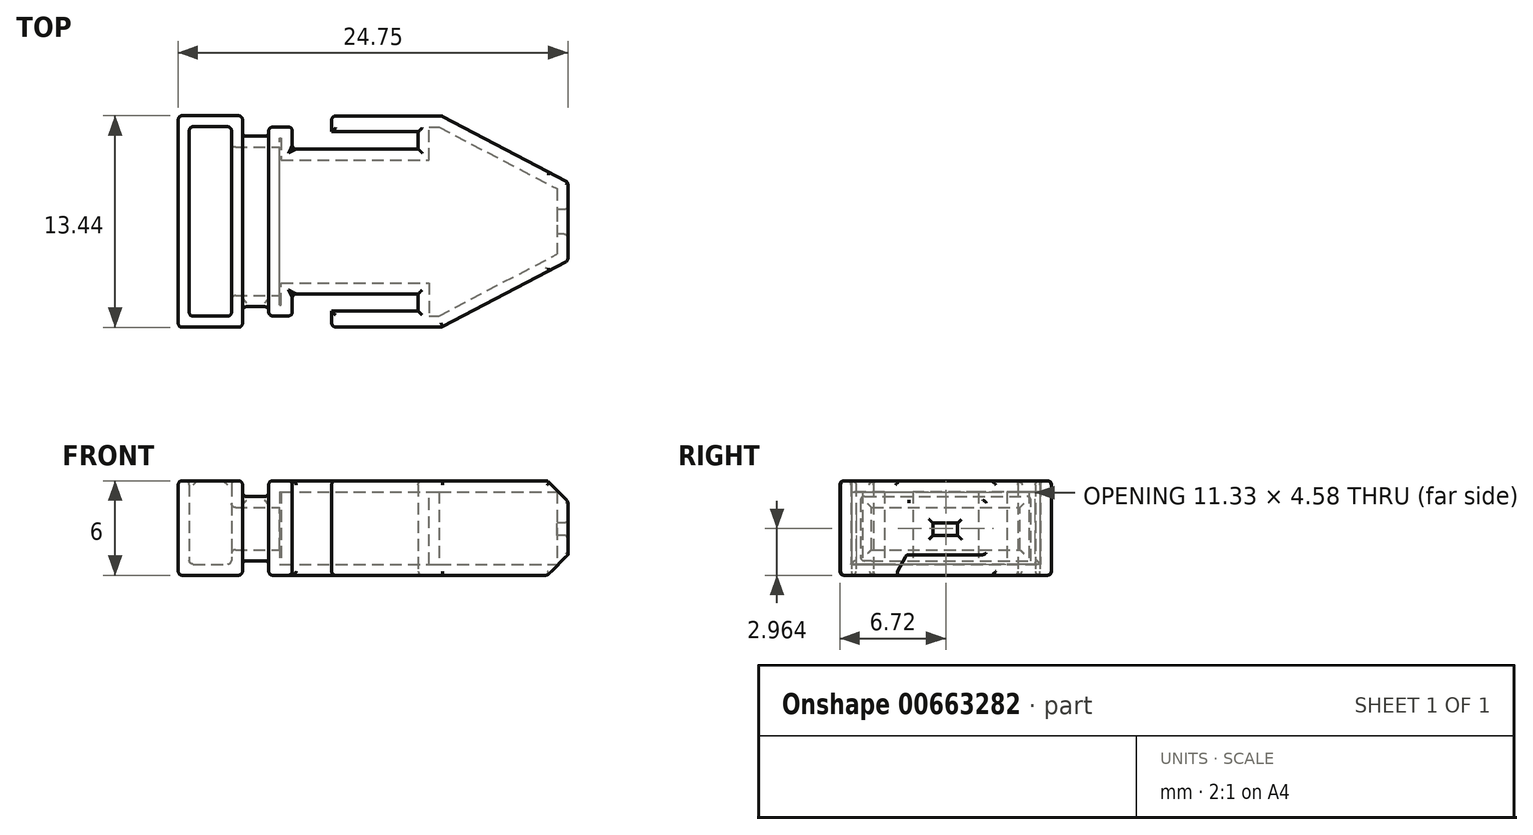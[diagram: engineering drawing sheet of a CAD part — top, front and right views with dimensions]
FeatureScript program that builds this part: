
annotation { "Feature Type Name" : "Feature", "Feature Type Description" : "" }
export const myFeature = defineFeature(function(context is Context, id is Id, definition is map)
    precondition{}
    {
        {
            var Q0;
            Q0=qCreatedBy(makeId("Top.planeOp"),FACE);
            var sketch = newSketch(context, id + "F0", { "sketchPlane" : qUnion([Q0])});
            skLineSegment(sketch, "E0", {"start": v(-19, 0) * mm, "end": v(-19, 6) * mm});
            skLineSegment(sketch, "E1", {"start": v(-19, 6) * mm, "end": v(-17.5, 6) * mm});
            skLineSegment(sketch, "E2", {"start": v(-17.5, 6) * mm, "end": v(-17.5, 4.6) * mm});
            skLineSegment(sketch, "E3", {"start": v(-17.5, 4.6) * mm, "end": v(-9.5, 4.6) * mm});
            skLineSegment(sketch, "E4", {"start": v(-9.5, 4.6) * mm, "end": v(-9.5, 5.7) * mm});
            skLineSegment(sketch, "E5", {"start": v(-9.5, 5.7) * mm, "end": v(-15, 5.7) * mm});
            skLineSegment(sketch, "E6", {"start": v(-15, 6.2) * mm, "end": v(-15, 5.7) * mm});
            skLineSegment(sketch, "E7", {"start": v(-15, 6.2) * mm, "end": v(-15, 6.2) * mm});
            skLineSegment(sketch, "E8", {"start": v(-15, 6.2) * mm, "end": v(-15, 6.7) * mm});
            skLineSegment(sketch, "E9", {"start": v(-15, 6.7) * mm, "end": v(-8, 6.7) * mm});
            skLineSegment(sketch, "E10", {"start": v(-8, 6.7) * mm, "end": v(0, 2.5) * mm});
            skLineSegment(sketch, "E11", {"start": v(0, 2.5) * mm, "end": v(0, 0) * mm});
            skLineSegment(sketch, "E12", {"start": v(0, 0) * mm, "end": v(-19, 0) * mm});
            skSolve(sketch);
        }
        {
            var Q0;
            Q0=makeQuery(id+"F0.imprint","IMPRINT",FACE,{"disambiguationData":[TD([[makeQuery(id+"F0.imprint","IMPRINT",EDGE,{"derivedFrom":sQuery(id+"F0.wireOp",EDGE,"E0")}),-1.0]])]});
            extrude(context, id + "F1", {"entities" : qUnion([Q0]), "depth" : 6 * mm, "offsetDistance" : 25 * mm});
        }
        {
            var Q0;
            Q0=makeQuery(id+"F1.opExtrude","SWEPT_FACE",FACE,{"disambiguationData":[OSD([sQuery(id+"F0.wireOp",EDGE,"E0")])]});
            var sketch = newSketch(context, id + "F2", { "sketchPlane" : qUnion([Q0])});
            skLineSegment(sketch, "E13.bottom", {"start": v(0, 0.92) * mm, "end": v(-5.41, 0.92) * mm});
            skLineSegment(sketch, "E13.top", {"start": v(0, 5) * mm, "end": v(-5.41, 5) * mm});
            skLineSegment(sketch, "E13.left", {"start": v(0, 0.92) * mm, "end": v(0, 5) * mm});
            skLineSegment(sketch, "E13.right", {"start": v(-5.41, 0.92) * mm, "end": v(-5.41, 5) * mm});
            skSolve(sketch);
        }
        {
            var Q0;
            Q0 = qSketchRegion(id + "F2", true);
            extrude(context, id + "F3", {"entities" : qUnion([Q0]), "operationType" : NewBodyOperationType.ADD, "depth" : 2 * mm, "offsetDistance" : 25 * mm});
        }
        {
            var Q0;
            Q0=qCreatedBy(makeId("Top.planeOp"),FACE);
            var sketch = newSketch(context, id + "F4", { "sketchPlane" : qUnion([Q0])});
            skLineSegment(sketch, "E14.bottom", {"start": v(-24.75, 6.72) * mm, "end": v(-20.67, 6.72) * mm});
            skLineSegment(sketch, "E14.top", {"start": v(-24.75, 0) * mm, "end": v(-20.67, 0) * mm});
            skLineSegment(sketch, "E14.left", {"start": v(-24.75, 6.72) * mm, "end": v(-24.75, 0) * mm});
            skLineSegment(sketch, "E14.right", {"start": v(-20.67, 6.72) * mm, "end": v(-20.67, 0) * mm});
            skSolve(sketch);
        }
        {
            var Q0;
            Q0 = qSketchRegion(id + "F4", true);
            extrude(context, id + "F5", {"entities" : qUnion([Q0]), "operationType" : NewBodyOperationType.ADD, "depth" : 6 * mm, "offsetDistance" : 25 * mm});
        }
        {
            var Q0;
            Q0=makeQuery(id+"F1.opExtrude","SWEPT_BODY",BODY,{"disambiguationData":[OSD([sQuery(id+"F0.wireOp",EDGE,"E0"),sQuery(id+"F0.wireOp",EDGE,"E1"),sQuery(id+"F0.wireOp",EDGE,"E2"),sQuery(id+"F0.wireOp",EDGE,"E3"),sQuery(id+"F0.wireOp",EDGE,"E4"),sQuery(id+"F0.wireOp",EDGE,"E5"),sQuery(id+"F0.wireOp",EDGE,"E6"),sQuery(id+"F0.wireOp",EDGE,"E8"),sQuery(id+"F0.wireOp",EDGE,"E9"),sQuery(id+"F0.wireOp",EDGE,"E10"),sQuery(id+"F0.wireOp",EDGE,"E11"),sQuery(id+"F0.wireOp",EDGE,"E12")])]});
            var Q1;
            Q1=makeQuery(id+"F5.boolean.opBoolean","MERGE",FACE,{"derivedFrom":[makeQuery(id+"F3.boolean.opBoolean","MERGE",FACE,{"derivedFrom":[makeQuery(id+"F1.opExtrude","SWEPT_FACE",FACE,{"disambiguationData":[OSD([sQuery(id+"F0.wireOp",EDGE,"E12")])]}),makeQuery(id+"F3.opExtrude","SWEPT_FACE",FACE,{"disambiguationData":[OSD([sQuery(id+"F2.wireOp",EDGE,"E13.left")])]})]}),makeQuery(id+"F5.opExtrude","SWEPT_FACE",FACE,{"disambiguationData":[OSD([sQuery(id+"F4.wireOp",EDGE,"E14.top")])]})]});
            mirror(context, id + "F6", {"operationType" : NewBodyOperationType.ADD, "entities" : qUnion([Q0]), "mirrorPlane" : qUnion([Q1])});
        }
        {
            var Q0;
            {var subQ0=makeQuery(id+"F5.opExtrude","CAP_FACE",FACE,{"disambiguationData":[OSD([sQuery(id+"F4.wireOp",EDGE,"E14.bottom"),sQuery(id+"F4.wireOp",EDGE,"E14.top"),sQuery(id+"F4.wireOp",EDGE,"E14.left"),sQuery(id+"F4.wireOp",EDGE,"E14.right")])],"isStart":false});Q0=makeQuery(id+"F6.boolean.opBoolean","MERGE",FACE,{"derivedFrom":[subQ0,makeQuery(id+"F6.opPattern","COPY",FACE,{"derivedFrom":subQ0,"instanceName":"1"})]});}
            shell(context, id + "F7", {"entities" : qUnion([Q0]), "thickness" : .7 * mm});
        }
        {
            var Q0;
            {var subQ0=makeQuery(id+"F1.opExtrude","CAP_EDGE",EDGE,{"disambiguationData":[OSD([sQuery(id+"F0.wireOp",EDGE,"E11")])],"isStart":false});Q0=makeQuery(id+"F6.boolean.opBoolean","MERGE",EDGE,{"derivedFrom":[subQ0,makeQuery(id+"F6.opPattern","COPY",EDGE,{"derivedFrom":subQ0,"instanceName":"1"})]});}
            chamfer(context, id + "F8", {"entities" : qUnion([Q0]), "width" : 1.3 * mm, "tangentPropagation" : true});
        }
        {
            var Q0;
            {var subQ0=makeQuery(id+"F1.opExtrude","CAP_EDGE",EDGE,{"disambiguationData":[OSD([sQuery(id+"F0.wireOp",EDGE,"E11")])],"isStart":true});Q0=makeQuery(id+"F6.boolean.opBoolean","MERGE",EDGE,{"derivedFrom":[subQ0,makeQuery(id+"F6.opPattern","COPY",EDGE,{"derivedFrom":subQ0,"instanceName":"1"})]});}
            chamfer(context, id + "F9", {"entities" : qUnion([Q0]), "width" : 1.3 * mm, "tangentPropagation" : true});
        }
        {
            var Q0;
            {var subQ0=makeQuery(id+"F5.opExtrude","SWEPT_FACE",FACE,{"disambiguationData":[OSD([sQuery(id+"F4.wireOp",EDGE,"E14.right")])]});Q0=makeQuery(id+"F6.boolean.opBoolean","MERGE",FACE,{"derivedFrom":[subQ0,makeQuery(id+"F6.opPattern","COPY",FACE,{"derivedFrom":subQ0,"instanceName":"1"})]});}
            var sketch = newSketch(context, id + "F10", { "sketchPlane" : qUnion([Q0])});
            skLineSegment(sketch, "E15.bottom", {"start": v(-0.81, 3.3) * mm, "end": v(0.76, 3.3) * mm});
            skLineSegment(sketch, "E15.top", {"start": v(-0.81, 2.54) * mm, "end": v(0.76, 2.54) * mm});
            skLineSegment(sketch, "E15.left", {"start": v(-0.81, 3.3) * mm, "end": v(-0.81, 2.54) * mm});
            skLineSegment(sketch, "E15.right", {"start": v(0.76, 3.3) * mm, "end": v(0.76, 2.54) * mm});
            skSolve(sketch);
        }
        {
            var Q0;
            Q0 = qSketchRegion(id + "F10", true);
            extrude(context, id + "F11", {"entities" : qUnion([Q0]), "operationType" : NewBodyOperationType.REMOVE, "depth" : 25 * mm, "offsetDistance" : 25 * mm});
        }
        {
            var Q0;
            {var subQ0=makeQuery(id+"F1.opExtrude","CAP_FACE",FACE,{"disambiguationData":[OSD([sQuery(id+"F0.wireOp",EDGE,"E0"),sQuery(id+"F0.wireOp",EDGE,"E1"),sQuery(id+"F0.wireOp",EDGE,"E2"),sQuery(id+"F0.wireOp",EDGE,"E3"),sQuery(id+"F0.wireOp",EDGE,"E4"),sQuery(id+"F0.wireOp",EDGE,"E5"),sQuery(id+"F0.wireOp",EDGE,"E6"),sQuery(id+"F0.wireOp",EDGE,"E8"),sQuery(id+"F0.wireOp",EDGE,"E9"),sQuery(id+"F0.wireOp",EDGE,"E10"),sQuery(id+"F0.wireOp",EDGE,"E11"),sQuery(id+"F0.wireOp",EDGE,"E12")])],"isStart":false});Q0=makeQuery(id+"F6.boolean.opBoolean","MERGE",FACE,{"derivedFrom":[subQ0,makeQuery(id+"F6.opPattern","COPY",FACE,{"derivedFrom":subQ0,"instanceName":"1"})]});}
            fillet(context, id + "F12", {"entities" : qUnion([Q0]), "radius" : .25 * mm, "tangentPropagation" : true, "allowEdgeOverflow" : false});
        }
        {
            var Q0;
            {var subQ0=makeQuery(id+"F1.opExtrude","CAP_FACE",FACE,{"disambiguationData":[OSD([sQuery(id+"F0.wireOp",EDGE,"E0"),sQuery(id+"F0.wireOp",EDGE,"E1"),sQuery(id+"F0.wireOp",EDGE,"E2"),sQuery(id+"F0.wireOp",EDGE,"E3"),sQuery(id+"F0.wireOp",EDGE,"E4"),sQuery(id+"F0.wireOp",EDGE,"E5"),sQuery(id+"F0.wireOp",EDGE,"E6"),sQuery(id+"F0.wireOp",EDGE,"E8"),sQuery(id+"F0.wireOp",EDGE,"E9"),sQuery(id+"F0.wireOp",EDGE,"E10"),sQuery(id+"F0.wireOp",EDGE,"E11"),sQuery(id+"F0.wireOp",EDGE,"E12")])],"isStart":true});Q0=makeQuery(id+"F6.boolean.opBoolean","MERGE",FACE,{"derivedFrom":[subQ0,makeQuery(id+"F6.opPattern","COPY",FACE,{"derivedFrom":subQ0,"instanceName":"1"})]});}
            var Q1;
            Q1=makeQuery(id+"F6.opPattern","COPY",EDGE,{"derivedFrom":makeQuery(id+"F1.opExtrude","SWEPT_EDGE",EDGE,{"disambiguationData":[OSD([sQuery(id+"F0.wireOp",EDGE,"E0"),sQuery(id+"F0.wireOp",EDGE,"E1")])]}),"instanceName":"1"});
            var Q2;
            Q2=makeQuery(id+"F6.opPattern","COPY",FACE,{"derivedFrom":makeQuery(id+"F3.opExtrude","SWEPT_FACE",FACE,{"disambiguationData":[OSD([sQuery(id+"F2.wireOp",EDGE,"E13.right")])]}),"instanceName":"1"});
            var Q3;
            {var subQ0=sQuery(id+"F0.wireOp",EDGE,"E0");var subQ1=makeQuery(id+"F1.opExtrude","SWEPT_FACE",FACE,{"disambiguationData":[OSD([subQ0])]});var subQ2=makeQuery(id+"F1.opExtrude","CAP_EDGE",EDGE,{"disambiguationData":[OSD([subQ0])],"isStart":false});Q3=makeQuery(id+"F12.opFillet","BLEND_EDGE",EDGE,{"blendedFrom":[makeQuery(id+"F6.boolean.opBoolean","MERGE",EDGE,{"derivedFrom":[subQ2,makeQuery(id+"F6.opPattern","COPY",EDGE,{"derivedFrom":subQ2,"instanceName":"1"})]}),makeQuery(id+"F6.boolean.opBoolean","MERGE",FACE,{"derivedFrom":[subQ1,makeQuery(id+"F6.opPattern","COPY",FACE,{"derivedFrom":subQ1,"instanceName":"1"})]})],"blendedInto":[makeQuery(id+"F6.boolean.opBoolean","MERGE",FACE,{"derivedFrom":[subQ1,makeQuery(id+"F6.opPattern","COPY",FACE,{"derivedFrom":subQ1,"instanceName":"1"})]})]});}
            var Q4;
            {var subQ0=makeQuery(id+"F5.boolean.opBoolean","INTERSECT",EDGE,{"derivedFrom":[makeQuery(id+"F3.opExtrude","SWEPT_FACE",FACE,{"disambiguationData":[OSD([sQuery(id+"F2.wireOp",EDGE,"E13.top")])]}),makeQuery(id+"F5.opExtrude","SWEPT_FACE",FACE,{"disambiguationData":[OSD([sQuery(id+"F4.wireOp",EDGE,"E14.right")])]})]});Q4=makeQuery(id+"F6.boolean.opBoolean","MERGE",EDGE,{"derivedFrom":[subQ0,makeQuery(id+"F6.opPattern","COPY",EDGE,{"derivedFrom":subQ0,"instanceName":"1"})]});}
            var Q5;
            {var subQ0=sQuery(id+"F0.wireOp",EDGE,"E0");var subQ1=makeQuery(id+"F1.opExtrude","SWEPT_FACE",FACE,{"disambiguationData":[OSD([subQ0])]});var subQ2=makeQuery(id+"F1.opExtrude","CAP_EDGE",EDGE,{"disambiguationData":[OSD([subQ0])],"isStart":false});Q5=makeQuery(id+"F12.opFillet","BLEND_EDGE",EDGE,{"blendedFrom":[makeQuery(id+"F6.boolean.opBoolean","MERGE",EDGE,{"derivedFrom":[subQ2,makeQuery(id+"F6.opPattern","COPY",EDGE,{"derivedFrom":subQ2,"instanceName":"1"})]}),makeQuery(id+"F6.boolean.opBoolean","MERGE",FACE,{"derivedFrom":[subQ1,makeQuery(id+"F6.opPattern","COPY",FACE,{"derivedFrom":subQ1,"instanceName":"1"})]})],"blendedInto":[makeQuery(id+"F6.boolean.opBoolean","MERGE",FACE,{"derivedFrom":[subQ1,makeQuery(id+"F6.opPattern","COPY",FACE,{"derivedFrom":subQ1,"instanceName":"1"})]})]});}
            var Q6;
            {var subQ0=makeQuery(id+"F3.opExtrude","SWEPT_FACE",FACE,{"disambiguationData":[OSD([sQuery(id+"F2.wireOp",EDGE,"E13.top")])]});Q6=makeQuery(id+"F6.boolean.opBoolean","MERGE",FACE,{"derivedFrom":[subQ0,makeQuery(id+"F6.opPattern","COPY",FACE,{"derivedFrom":subQ0,"instanceName":"1"})]});}
            var Q7;
            Q7=makeQuery(id+"F8.opChamfer","BLEND_FACE",FACE,{"disambiguationData":[OSD([sQuery(id+"F0.wireOp",EDGE,"E11")])]});
            var Q8;
            Q8=makeQuery(id+"F6.opPattern","COPY",EDGE,{"derivedFrom":makeQuery(id+"F1.opExtrude","SWEPT_EDGE",EDGE,{"disambiguationData":[OSD([sQuery(id+"F0.wireOp",EDGE,"E8"),sQuery(id+"F0.wireOp",EDGE,"E9")])]}),"instanceName":"1"});
            var Q9;
            Q9=makeQuery(id+"F6.opPattern","COPY",EDGE,{"derivedFrom":makeQuery(id+"F1.opExtrude","SWEPT_EDGE",EDGE,{"disambiguationData":[OSD([sQuery(id+"F0.wireOp",EDGE,"E10"),sQuery(id+"F0.wireOp",EDGE,"E11")])]}),"instanceName":"1"});
            var Q10;
            Q10=makeQuery(id+"F6.opPattern","COPY",EDGE,{"derivedFrom":makeQuery(id+"F5.opExtrude","SWEPT_EDGE",EDGE,{"disambiguationData":[OSD([sQuery(id+"F4.wireOp",EDGE,"E14.bottom"),sQuery(id+"F4.wireOp",EDGE,"E14.left")])]}),"instanceName":"1"});
            var Q11;
            Q11=makeQuery(id+"F6.opPattern","COPY",FACE,{"derivedFrom":makeQuery(id+"F5.opExtrude","SWEPT_FACE",FACE,{"disambiguationData":[OSD([sQuery(id+"F4.wireOp",EDGE,"E14.bottom")])]}),"instanceName":"1"});
            fillet(context, id + "F13", {"entities" : qUnion([Q0, Q1, Q2, Q3, Q4, Q5, Q6, Q7, Q8, Q9, Q10, Q11]), "radius" : .25 * mm, "tangentPropagation" : true, "allowEdgeOverflow" : false});
        }
        {
            var Q0;
            Q0=makeQuery(id+"F1.opExtrude","SWEPT_FACE",FACE,{"disambiguationData":[OSD([sQuery(id+"F0.wireOp",EDGE,"E10")])]});
            var Q1;
            Q1=makeQuery(id+"F1.opExtrude","SWEPT_FACE",FACE,{"disambiguationData":[OSD([sQuery(id+"F0.wireOp",EDGE,"E9")])]});
            var Q2;
            {var subQ0=makeQuery(id+"F5.opExtrude","CAP_EDGE",EDGE,{"disambiguationData":[OSD([sQuery(id+"F4.wireOp",EDGE,"E14.right")])],"isStart":false});Q2=makeQuery(id+"F6.boolean.opBoolean","MERGE",EDGE,{"derivedFrom":[subQ0,makeQuery(id+"F6.opPattern","COPY",EDGE,{"derivedFrom":subQ0,"instanceName":"1"})]});}
            fillet(context, id + "F14", {"entities" : qUnion([Q0, Q1, Q2]), "radius" : .25 * mm, "tangentPropagation" : true, "allowEdgeOverflow" : false});
        }
        {
            var Q0;
            {var subQ0=makeQuery(id+"F5.opExtrude","CAP_EDGE",EDGE,{"disambiguationData":[OSD([sQuery(id+"F4.wireOp",EDGE,"E14.left")])],"isStart":false});Q0=makeQuery(id+"F6.boolean.opBoolean","MERGE",EDGE,{"derivedFrom":[subQ0,makeQuery(id+"F6.opPattern","COPY",EDGE,{"derivedFrom":subQ0,"instanceName":"1"})]});}
            var Q1;
            Q1=makeQuery(id+"F7.opShell","OFFSET_FACE",FACE,{"disambiguationData":[OSD([sQuery(id+"F4.wireOp",EDGE,"E14.left")])]});
            var Q2;
            Q2=makeQuery(id+"F7.opShell","OFFSET_FACE",FACE,{"disambiguationData":[OSD([sQuery(id+"F4.wireOp",EDGE,"E14.right")])]});
            var Q3;
            Q3=makeQuery(id+"F5.opExtrude","CAP_EDGE",EDGE,{"disambiguationData":[OSD([sQuery(id+"F4.wireOp",EDGE,"E14.bottom")])],"isStart":true});
            var Q4;
            Q4=makeQuery(id+"F5.opExtrude","SWEPT_EDGE",EDGE,{"disambiguationData":[OSD([sQuery(id+"F4.wireOp",EDGE,"E14.bottom"),sQuery(id+"F4.wireOp",EDGE,"E14.left")])]});
            var Q5;
            {var subQ0=makeQuery(id+"F5.opExtrude","CAP_EDGE",EDGE,{"disambiguationData":[OSD([sQuery(id+"F4.wireOp",EDGE,"E14.left")])],"isStart":true});Q5=makeQuery(id+"F6.boolean.opBoolean","MERGE",EDGE,{"derivedFrom":[subQ0,makeQuery(id+"F6.opPattern","COPY",EDGE,{"derivedFrom":subQ0,"instanceName":"1"})]});}
            var Q6;
            {var subQ0=makeQuery(id+"F1.opExtrude","SWEPT_FACE",FACE,{"disambiguationData":[OSD([sQuery(id+"F0.wireOp",EDGE,"E11")])]});Q6=makeQuery(id+"F11.boolean.opBoolean","INTERSECT",EDGE,{"derivedFrom":[makeQuery(id+"F6.boolean.opBoolean","MERGE",FACE,{"derivedFrom":[subQ0,makeQuery(id+"F6.opPattern","COPY",FACE,{"derivedFrom":subQ0,"instanceName":"1"})]}),makeQuery(id+"F11.opExtrude","SWEPT_FACE",FACE,{"disambiguationData":[OSD([sQuery(id+"F10.wireOp",EDGE,"E15.top")])]})]});}
            var Q7;
            {var subQ0=makeQuery(id+"F1.opExtrude","SWEPT_FACE",FACE,{"disambiguationData":[OSD([sQuery(id+"F0.wireOp",EDGE,"E11")])]});Q7=makeQuery(id+"F11.boolean.opBoolean","INTERSECT",EDGE,{"derivedFrom":[makeQuery(id+"F6.boolean.opBoolean","MERGE",FACE,{"derivedFrom":[subQ0,makeQuery(id+"F6.opPattern","COPY",FACE,{"derivedFrom":subQ0,"instanceName":"1"})]}),makeQuery(id+"F11.opExtrude","SWEPT_FACE",FACE,{"disambiguationData":[OSD([sQuery(id+"F10.wireOp",EDGE,"E15.right")])]})]});}
            var Q8;
            {var subQ0=makeQuery(id+"F1.opExtrude","SWEPT_FACE",FACE,{"disambiguationData":[OSD([sQuery(id+"F0.wireOp",EDGE,"E11")])]});Q8=makeQuery(id+"F11.boolean.opBoolean","INTERSECT",EDGE,{"derivedFrom":[makeQuery(id+"F6.boolean.opBoolean","MERGE",FACE,{"derivedFrom":[subQ0,makeQuery(id+"F6.opPattern","COPY",FACE,{"derivedFrom":subQ0,"instanceName":"1"})]}),makeQuery(id+"F11.opExtrude","SWEPT_FACE",FACE,{"disambiguationData":[OSD([sQuery(id+"F10.wireOp",EDGE,"E15.bottom")])]})]});}
            var Q9;
            {var subQ0=makeQuery(id+"F1.opExtrude","SWEPT_FACE",FACE,{"disambiguationData":[OSD([sQuery(id+"F0.wireOp",EDGE,"E11")])]});Q9=makeQuery(id+"F11.boolean.opBoolean","INTERSECT",EDGE,{"derivedFrom":[makeQuery(id+"F6.boolean.opBoolean","MERGE",FACE,{"derivedFrom":[subQ0,makeQuery(id+"F6.opPattern","COPY",FACE,{"derivedFrom":subQ0,"instanceName":"1"})]}),makeQuery(id+"F11.opExtrude","SWEPT_FACE",FACE,{"disambiguationData":[OSD([sQuery(id+"F10.wireOp",EDGE,"E15.left")])]})]});}
            fillet(context, id + "F15", {"entities" : qUnion([Q0, Q1, Q2, Q3, Q4, Q5, Q6, Q7, Q8, Q9]), "radius" : .25 * mm, "tangentPropagation" : true, "allowEdgeOverflow" : false});
        }
        {
            var Q0;
            Q0=makeQuery(id+"F6.opPattern","COPY",EDGE,{"derivedFrom":makeQuery(id+"F1.opExtrude","SWEPT_EDGE",EDGE,{"disambiguationData":[OSD([sQuery(id+"F0.wireOp",EDGE,"E1"),sQuery(id+"F0.wireOp",EDGE,"E2")])]}),"instanceName":"1"});
            var Q1;
            Q1=makeQuery(id+"F6.opPattern","COPY",EDGE,{"derivedFrom":makeQuery(id+"F1.opExtrude","SWEPT_EDGE",EDGE,{"disambiguationData":[OSD([sQuery(id+"F0.wireOp",EDGE,"E2"),sQuery(id+"F0.wireOp",EDGE,"E3")])]}),"instanceName":"1"});
            fillet(context, id + "F16", {"entities" : qUnion([Q0, Q1]), "radius" : .25 * mm, "tangentPropagation" : true, "allowEdgeOverflow" : false});
        }
        {
            var Q0;
            Q0=makeQuery(id+"F1.opExtrude","SWEPT_FACE",FACE,{"disambiguationData":[OSD([sQuery(id+"F0.wireOp",EDGE,"E1")])]});
            var Q1;
            Q1=makeQuery(id+"F1.opExtrude","SWEPT_EDGE",EDGE,{"disambiguationData":[OSD([sQuery(id+"F0.wireOp",EDGE,"E2"),sQuery(id+"F0.wireOp",EDGE,"E3")])]});
            var Q2;
            Q2=makeQuery(id+"F5.opExtrude","SWEPT_EDGE",EDGE,{"disambiguationData":[OSD([sQuery(id+"F4.wireOp",EDGE,"E14.bottom"),sQuery(id+"F4.wireOp",EDGE,"E14.right")])]});
            var Q3;
            Q3=makeQuery(id+"F5.opExtrude","CAP_EDGE",EDGE,{"disambiguationData":[OSD([sQuery(id+"F4.wireOp",EDGE,"E14.bottom")])],"isStart":false});
            fillet(context, id + "F17", {"entities" : qUnion([Q0, Q1, Q2, Q3]), "radius" : .25 * mm, "tangentPropagation" : true, "allowEdgeOverflow" : false});
        }
        {
            var Q0;
            Q0=makeQuery(id+"F6.opPattern","COPY",EDGE,{"derivedFrom":makeQuery(id+"F1.opExtrude","SWEPT_EDGE",EDGE,{"disambiguationData":[OSD([sQuery(id+"F0.wireOp",EDGE,"E9"),sQuery(id+"F0.wireOp",EDGE,"E10")])]}),"instanceName":"1"});
            fillet(context, id + "F18", {"entities" : qUnion([Q0]), "radius" : .25 * mm, "tangentPropagation" : true, "allowEdgeOverflow" : false});
        }
    });
